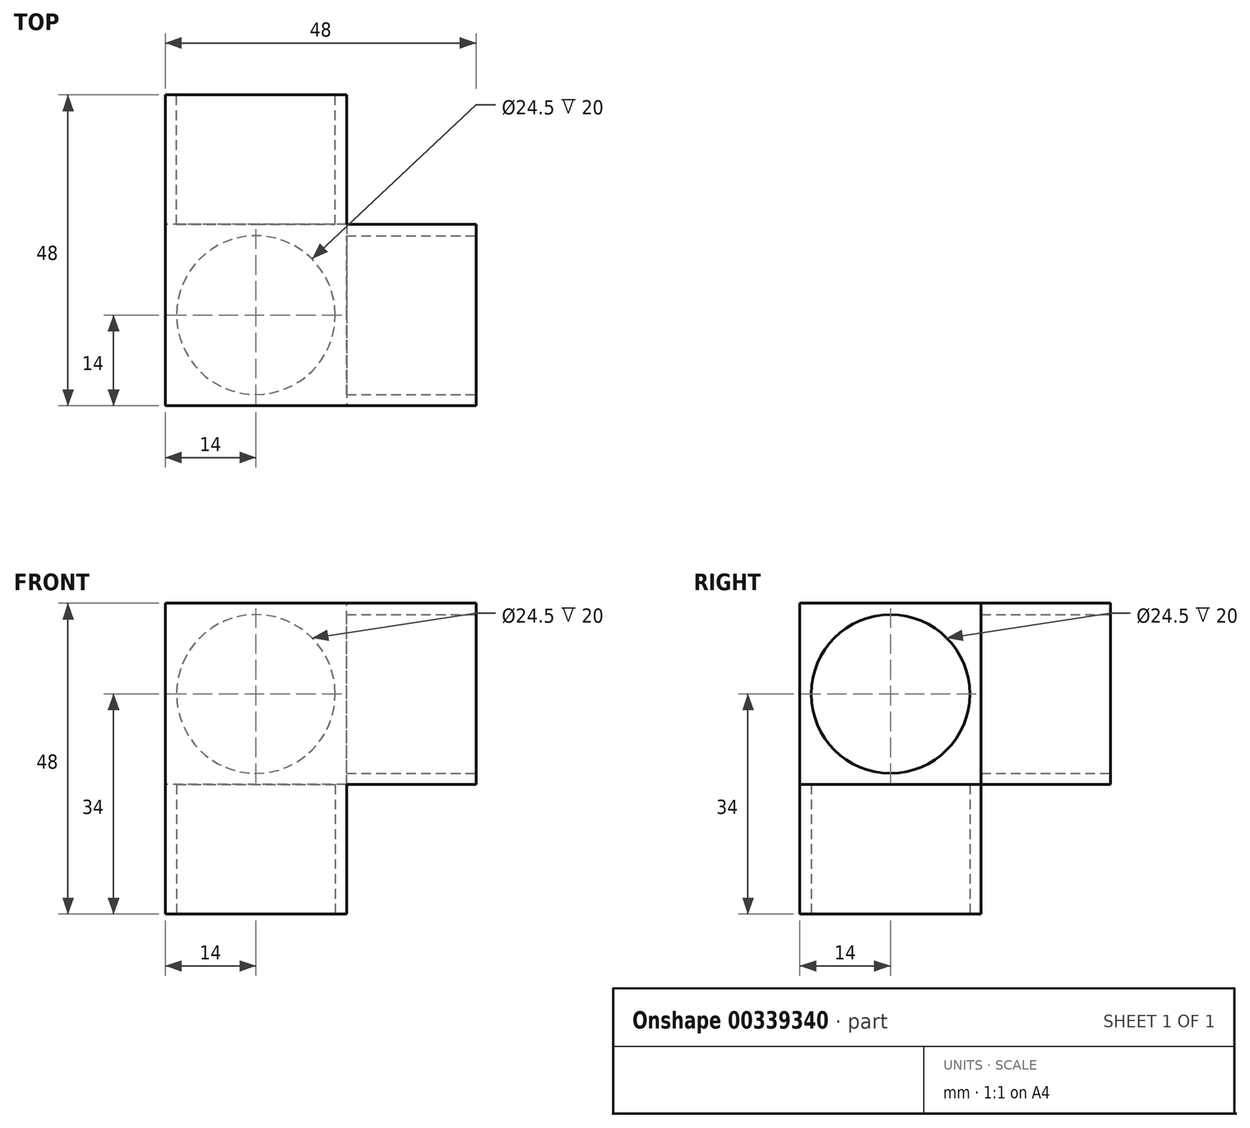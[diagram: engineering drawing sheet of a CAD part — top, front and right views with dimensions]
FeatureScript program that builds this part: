
annotation { "Feature Type Name" : "Feature", "Feature Type Description" : "" }
export const myFeature = defineFeature(function(context is Context, id is Id, definition is map)
    precondition{}
    {
        {
            var Q0;
            Q0=qCreatedBy(makeId("Right.planeOp"),FACE);
            var sketch = newSketch(context, id + "F0", { "sketchPlane" : qUnion([Q0])});
            skLineSegment(sketch, "E0.bottom", {"start": v(14, 14) * mm, "end": v(-14, 14) * mm});
            skLineSegment(sketch, "E0.top", {"start": v(14, -14) * mm, "end": v(-14, -14) * mm});
            skLineSegment(sketch, "E0.left", {"start": v(14, 14) * mm, "end": v(14, -14) * mm});
            skLineSegment(sketch, "E0.right", {"start": v(-14, 14) * mm, "end": v(-14, -14) * mm});
            skPoint(sketch, "E0.middle", {"position": v(0, 0) * mm});
            skSolve(sketch);
        }
        {
            var Q0;
            Q0=makeQuery(id+"F0.imprint","IMPRINT",FACE,{"disambiguationData":[TD([[makeQuery(id+"F0.imprint","IMPRINT",EDGE,{"derivedFrom":sQuery(id+"F0.wireOp",EDGE,"E0.bottom")}),1.0]])]});
            extrude(context, id + "F1", {"entities" : qUnion([Q0]), "depth" : 48 * mm});
        }
        {
            var Q0;
            Q0=makeQuery(id+"F1.opExtrude","SWEPT_FACE",FACE,{"disambiguationData":[OSD([sQuery(id+"F0.wireOp",EDGE,"E0.right")])]});
            var sketch = newSketch(context, id + "F2", { "sketchPlane" : qUnion([Q0])});
            skLineSegment(sketch, "E1.bottom", {"start": v(0, 14) * mm, "end": v(28, 14) * mm});
            skLineSegment(sketch, "E1.top", {"start": v(0, -14) * mm, "end": v(28, -14) * mm});
            skLineSegment(sketch, "E1.left", {"start": v(0, 14) * mm, "end": v(0, -14) * mm});
            skLineSegment(sketch, "E1.right", {"start": v(28, 14) * mm, "end": v(28, -14) * mm});
            skSolve(sketch);
        }
        {
            var Q0;
            Q0=makeQuery(id+"F2.imprint","IMPRINT",FACE,{"disambiguationData":[TD([[makeQuery(id+"F2.imprint","IMPRINT",EDGE,{"derivedFrom":sQuery(id+"F2.wireOp",EDGE,"E1.bottom")}),1.0]])]});
            extrude(context, id + "F3", {"entities" : qUnion([Q0]), "operationType" : NewBodyOperationType.ADD, "oppositeDirection" : true, "depth" : 48 * mm});
        }
        {
            var Q0;
            Q0=makeQuery(id+"F3.boolean.opBoolean","MERGE",FACE,{"derivedFrom":[makeQuery(id+"F1.opExtrude","SWEPT_FACE",FACE,{"disambiguationData":[OSD([sQuery(id+"F0.wireOp",EDGE,"E0.bottom")])]}),makeQuery(id+"F3.opExtrude","SWEPT_FACE",FACE,{"disambiguationData":[OSD([sQuery(id+"F2.wireOp",EDGE,"E1.bottom")])]})]});
            var sketch = newSketch(context, id + "F4", { "sketchPlane" : qUnion([Q0])});
            skLineSegment(sketch, "E2.bottom", {"start": v(0, -14) * mm, "end": v(28, -14) * mm});
            skLineSegment(sketch, "E2.top", {"start": v(0, 14) * mm, "end": v(28, 14) * mm});
            skLineSegment(sketch, "E2.left", {"start": v(0, -14) * mm, "end": v(0, 14) * mm});
            skLineSegment(sketch, "E2.right", {"start": v(28, -14) * mm, "end": v(28, 14) * mm});
            skSolve(sketch);
        }
        {
            var Q0;
            Q0=makeQuery(id+"F4.imprint","IMPRINT",FACE,{"disambiguationData":[TD([[makeQuery(id+"F4.imprint","IMPRINT",EDGE,{"derivedFrom":sQuery(id+"F4.wireOp",EDGE,"E2.bottom")}),-1.0]])]});
            extrude(context, id + "F5", {"entities" : qUnion([Q0]), "operationType" : NewBodyOperationType.ADD, "oppositeDirection" : true, "depth" : 48 * mm});
        }
        {
            var Q0;
            Q0=makeQuery(id+"F1.opExtrude","CAP_FACE",FACE,{"disambiguationData":[OSD([sQuery(id+"F0.wireOp",EDGE,"E0.bottom"),sQuery(id+"F0.wireOp",EDGE,"E0.top"),sQuery(id+"F0.wireOp",EDGE,"E0.left"),sQuery(id+"F0.wireOp",EDGE,"E0.right")])],"isStart":false});
            var sketch = newSketch(context, id + "F6", { "sketchPlane" : qUnion([Q0])});
            skCircle(sketch, "E3", {"center": v(0, 0) * mm, "radius": 12.25 * mm});
            skSolve(sketch);
        }
        {
            var Q0;
            Q0=makeQuery(id+"F6.imprint","IMPRINT",FACE,{"disambiguationData":[TD([[makeQuery(id+"F6.imprint","IMPRINT",EDGE,{"derivedFrom":sQuery(id+"F6.wireOp",EDGE,"E3")}),1.0]])]});
            extrude(context, id + "F7", {"entities" : qUnion([Q0]), "operationType" : NewBodyOperationType.REMOVE, "oppositeDirection" : true, "depth" : 20 * mm});
        }
        {
            var Q0;
            Q0=makeQuery(id+"F3.opExtrude","CAP_FACE",FACE,{"disambiguationData":[OSD([sQuery(id+"F2.wireOp",EDGE,"E1.bottom"),sQuery(id+"F2.wireOp",EDGE,"E1.top"),sQuery(id+"F2.wireOp",EDGE,"E1.left"),sQuery(id+"F2.wireOp",EDGE,"E1.right")])],"isStart":false});
            var sketch = newSketch(context, id + "F8", { "sketchPlane" : qUnion([Q0])});
            skCircle(sketch, "E4", {"center": v(-14, 0) * mm, "radius": 12.25 * mm});
            skSolve(sketch);
        }
        {
            var Q0;
            Q0=makeQuery(id+"F8.imprint","IMPRINT",FACE,{"disambiguationData":[TD([[makeQuery(id+"F8.imprint","IMPRINT",EDGE,{"derivedFrom":sQuery(id+"F8.wireOp",EDGE,"E4")}),1.0]])]});
            extrude(context, id + "F9", {"entities" : qUnion([Q0]), "operationType" : NewBodyOperationType.REMOVE, "oppositeDirection" : true, "depth" : 20 * mm});
        }
        {
            var Q0;
            Q0=makeQuery(id+"F5.opExtrude","CAP_FACE",FACE,{"disambiguationData":[OSD([sQuery(id+"F4.wireOp",EDGE,"E2.bottom"),sQuery(id+"F4.wireOp",EDGE,"E2.top"),sQuery(id+"F4.wireOp",EDGE,"E2.left"),sQuery(id+"F4.wireOp",EDGE,"E2.right")])],"isStart":false});
            var sketch = newSketch(context, id + "F10", { "sketchPlane" : qUnion([Q0])});
            skCircle(sketch, "E5", {"center": v(14, 0) * mm, "radius": 12.25 * mm});
            skSolve(sketch);
        }
        {
            var Q0;
            Q0=makeQuery(id+"F10.imprint","IMPRINT",FACE,{"disambiguationData":[TD([[makeQuery(id+"F10.imprint","IMPRINT",EDGE,{"derivedFrom":sQuery(id+"F10.wireOp",EDGE,"E5")}),1.0]])]});
            extrude(context, id + "F11", {"entities" : qUnion([Q0]), "operationType" : NewBodyOperationType.REMOVE, "oppositeDirection" : true, "depth" : 20 * mm});
        }
    });
